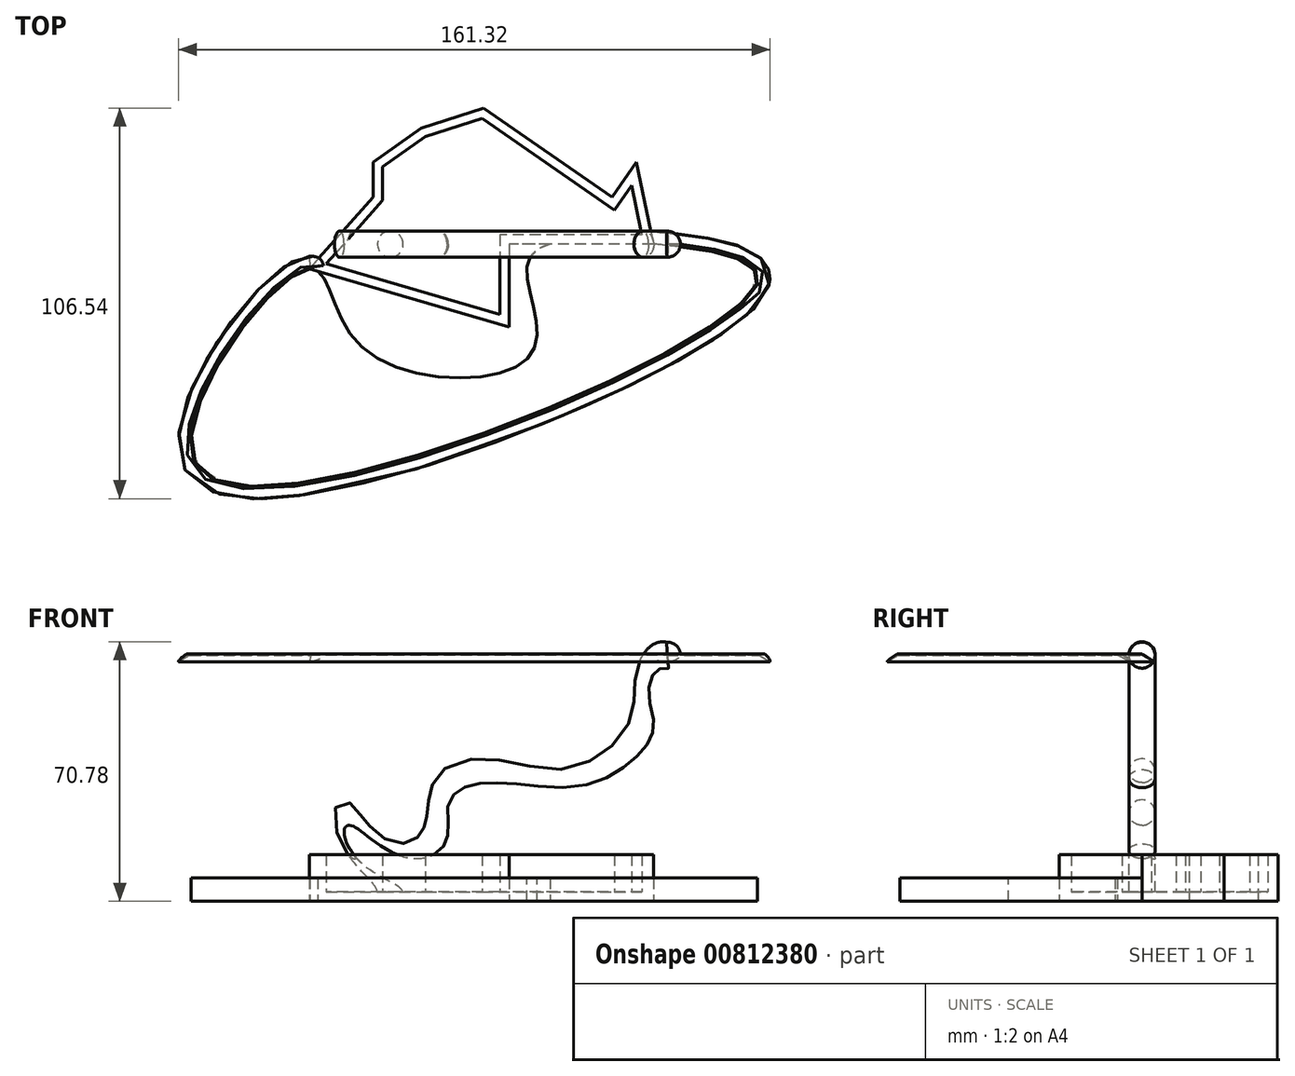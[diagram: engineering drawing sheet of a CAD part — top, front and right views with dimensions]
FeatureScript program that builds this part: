
annotation { "Feature Type Name" : "Feature", "Feature Type Description" : "" }
export const myFeature = defineFeature(function(context is Context, id is Id, definition is map)
    precondition{}
    {
        {
            var Q0;
            Q0=qCreatedBy(makeId("Top.planeOp"),FACE);
            var sketch = newSketch(context, id + "F0", { "sketchPlane" : qUnion([Q0])});
            skLineSegment(sketch, "E0", {"start": v(-24.02, 31.68) * mm, "end": v(-7, 37.1) * mm});
            skLineSegment(sketch, "E1", {"start": v(-7, 37.1) * mm, "end": v(28.1, 12.86) * mm});
            skLineSegment(sketch, "E2", {"start": v(28.1, 12.86) * mm, "end": v(34.66, 22.35) * mm});
            skLineSegment(sketch, "E3", {"start": v(34.66, 22.35) * mm, "end": v(39.33, 0) * mm});
            skLineSegment(sketch, "E4", {"start": v(39.33, 0) * mm, "end": v(0, 0) * mm});
            skLineSegment(sketch, "E5", {"start": v(0, 0) * mm, "end": v(0, -22.62) * mm});
            skLineSegment(sketch, "E6", {"start": v(0, -22.62) * mm, "end": v(-54.43, -6.69) * mm});
            skLineSegment(sketch, "E7", {"start": v(-54.43, -6.69) * mm, "end": v(-37.05, 12.86) * mm});
            skLineSegment(sketch, "E8", {"start": v(-37.05, 12.86) * mm, "end": v(-37.05, 22.35) * mm});
            skLineSegment(sketch, "E9", {"start": v(-37.05, 22.35) * mm, "end": v(-24.02, 31.68) * mm});
            skSolve(sketch);
        }
        {
            var Q0;
            Q0 = qSketchRegion(id + "F0", true);
            extrude(context, id + "F1", {"entities" : qUnion([Q0]), "depth" : 12.7 * mm, "offsetDistance" : 25.4 * mm});
        }
        {
            var Q0;
            Q0=makeQuery(id+"F1.opExtrude","CAP_FACE",FACE,{"disambiguationData":[OSD([sQuery(id+"F0.wireOp",EDGE,"E0"),sQuery(id+"F0.wireOp",EDGE,"E1"),sQuery(id+"F0.wireOp",EDGE,"E2"),sQuery(id+"F0.wireOp",EDGE,"E3"),sQuery(id+"F0.wireOp",EDGE,"E4"),sQuery(id+"F0.wireOp",EDGE,"E5"),sQuery(id+"F0.wireOp",EDGE,"E6"),sQuery(id+"F0.wireOp",EDGE,"E7"),sQuery(id+"F0.wireOp",EDGE,"E8"),sQuery(id+"F0.wireOp",EDGE,"E9")])],"isStart":false});
            shell(context, id + "F2", {"entities" : qUnion([Q0]), "thickness" : 2.54 * mm});
        }
        {
            var Q0;
            Q0=qCreatedBy(makeId("Front.planeOp"),FACE);
            var sketch = newSketch(context, id + "F3", { "sketchPlane" : qUnion([Q0])});
            skLineSegment(sketch, "E10", {"start": v(-32.33, 0) * mm, "end": v(-32.33, 21.1) * mm});
            skFitSpline(sketch, "E11", {"points": [v(-32.33, 21.1) * mm, v(-28.14, 28.57) * mm, v(-18.31, 29.25) * mm, v(-4.05, 40.56) * mm, v(26.9, 47.83) * mm, v(51.63, 68.22) * mm, v(64.2, 68.8) * mm], "startDerivative": vector(24.65, 83.62) * mm, "endDerivative": vector(87.47, -18.4) * mm});
            skSolve(sketch);
        }
        {
            var Q0;
            Q0=qCreatedBy(makeId("Top.planeOp"),FACE);
            var sketch = newSketch(context, id + "F4", { "sketchPlane" : qUnion([Q0])});
            skCircle(sketch, "E12", {"center": v(-32.33, 0) * mm, "radius": 3.56 * mm});
            skSolve(sketch);
        }
        {
            var Q0;
            Q0 = qSketchRegion(id + "F4", true);
            var Q1;
            Q1=sQuery(id+"F3.wireOp",EDGE,"E11");
            sweep(context, id + "F5", {"operationType" : NewBodyOperationType.ADD, "profiles" : qUnion([Q0]), "path" : qUnion([Q1])});
        }
        {
            var Q0;
            Q0=qCreatedBy(makeId("Top.planeOp"),FACE);
            var sketch = newSketch(context, id + "F6", { "sketchPlane" : qUnion([Q0])});
            skFitSpline(sketch, "E13", {"points": [v(5.16, -4.77) * mm, v(6.06, -29.88) * mm, v(-40.71, -27.63) * mm, v(-55.1, -6.82) * mm, v(-84.29, -61.43) * mm, v(66.9, -11.87) * mm, v(39.94, 0) * mm, v(5.16, -4.77) * mm]});
            skSolve(sketch);
        }
        {
            var Q0;
            Q0 = qSketchRegion(id + "F6", true);
            extrude(context, id + "F7", {"entities" : qUnion([Q0]), "operationType" : NewBodyOperationType.ADD, "depth" : 6.35 * mm, "offsetDistance" : 25.4 * mm});
        }
        {
            var Q0;
            Q0=makeQuery(id+"F5.opSweep","CAP_FACE",FACE,{"disambiguationData":[OSD([sQuery(id+"F3.wireOp",VERTEX,"E11.end"),sQuery(id+"F4.wireOp",EDGE,"E12")])],"isStart":false});
            var sketch = newSketch(context, id + "F8", { "sketchPlane" : qUnion([Q0])});
            skCircle(sketch, "E14", {"center": v(0, 63.5) * mm, "radius": 3.54 * mm});
            skLineSegment(sketch, "E15", {"start": v(-3.56, 63.5) * mm, "end": v(3.56, 63.5) * mm});
            skSolve(sketch);
        }
        {
            var Q0;
            {var subQ0=sQuery(id+"F8.wireOp",EDGE,"E15");var subQ1=sQuery(id+"F8.wireOp",EDGE,"E14");var subQ2=makeQuery(id+"F8.imprint","INTERSECT",VERTEX,{"disambiguationData":[OD(0.0)],"derivedFrom":[subQ1,subQ0]});Q0=makeQuery(id+"F8.imprint","IMPRINT",FACE,{"disambiguationData":[TD([[makeQuery(id+"F8.imprint","IMPRINT",EDGE,{"disambiguationData":[TD([[subQ2,1.0]])],"derivedFrom":subQ1}),1.0]])]});}
            var Q1;
            Q1=sQuery(id+"F8.wireOp",EDGE,"E15");
            revolve(context, id + "F9", {"operationType" : NewBodyOperationType.ADD, "surfaceOperationType" : NewSurfaceOperationType.NEW, "entities" : qUnion([Q0]), "axis" : qUnion([Q1]), "revolveType" : RevolveType.ONE_DIRECTION, "angle" : 90 * degree});
        }
        {
            var Q0;
            Q0=makeQuery(id+"F9.opRevolve","CAP_FACE",FACE,{"disambiguationData":[OSD([sQuery(id+"F8.wireOp",EDGE,"E14"),sQuery(id+"F8.wireOp",EDGE,"E15")])],"isStart":false});
            var sketch = newSketch(context, id + "F10", { "sketchPlane" : qUnion([Q0])});
            skLineSegment(sketch, "E16", {"start": v(51.88, 0) * mm, "end": v(48.34, 0) * mm});
            skSolve(sketch);
        }
        {
            var Q0;
            {var subQ0=sQuery(id+"F10.wireOp",EDGE,"E16");Q0=makeQuery(id+"F10.imprint","IMPRINT",FACE,{"disambiguationData":[TD([[makeQuery(id+"F10.imprint","IMPRINT",EDGE,{"derivedFrom":subQ0}),1.0]])]});}
            var Q1;
            Q1=sQuery(id+"F10.wireOp",EDGE,"E16");
            revolve(context, id + "F11", {"operationType" : NewBodyOperationType.ADD, "surfaceOperationType" : NewSurfaceOperationType.NEW, "entities" : qUnion([Q0]), "axis" : qUnion([Q1]), "revolveType" : RevolveType.ONE_DIRECTION, "angle" : 30 * degree});
        }
        {
            var Q0;
            Q0=makeQuery(id+"F11.opRevolve","CAP_FACE",FACE,{"disambiguationData":[OSD([sQuery(id+"F8.wireOp",EDGE,"E14"),sQuery(id+"F8.wireOp",EDGE,"E15"),sQuery(id+"F10.wireOp",EDGE,"E16")])],"isStart":false});
            var Q1;
            {var subQ0=sQuery(id+"F6.wireOp",EDGE,"E13");var subQ2=sQuery(id+"F0.wireOp",EDGE,"E3");Q1=makeQuery(id+"F7.boolean.opBoolean","SPLIT",EDGE,{"disambiguationData":[TD([makeQuery(id+"F1.opExtrude","SWEPT_FACE",FACE,{"disambiguationData":[OSD([subQ2])]})])],"derivedFrom":makeQuery(id+"F7.opExtrude","CAP_EDGE",EDGE,{"disambiguationData":[OSD([subQ0])],"isStart":true})});}
            sweep(context, id + "F12", {"operationType" : NewBodyOperationType.ADD, "profiles" : qUnion([Q0]), "path" : qUnion([Q1])});
        }
    });
